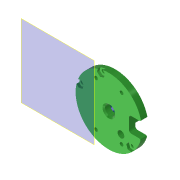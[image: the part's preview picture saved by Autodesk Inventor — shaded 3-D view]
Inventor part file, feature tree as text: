
AUTODESK INVENTOR PART (.ipt)
format: ipt  version: 2022 (Build 260153000, 153)  size: 526,848 bytes
history: native  units: in
note: dims shown in document units (in); Inventor stores cm internally (conversion verified against a paired STEP export)
features: reference x11, extrude x9, sketch x8, other x6, plane x4, projected_geometry x2, fillet x1, chamfer x1
ambient origin geometry x8: Origin, YZ Plane, XZ Plane, XY Plane, X Axis, Y Axis, Z Axis, Center Point
bodies: Solid1 (feature_tree)
feature tree (42):
  plane  "Work Plane1"
  extrude  "Extrusion1"  Depth=0.315in
  extrude  "Extrusion2"  Depth=1.0in
  plane  "Arbeitsebene4"
  extrude  "Extrusion5"  TaperAngle=0.0deg  [1 undecoded]
  plane  "Arbeitsebene3"
  extrude  "Extrusion6"  Depth=0.1102in
  plane  "Arbeitsebene2"
  extrude  "Extrusion7"  Depth=0.0787in
  extrude  "Extrusion10"  Depth=0.0394in TaperAngle=0.0deg
  extrude  "Extrusion11"  Depth=0.3937in
  extrude  "Extrusion12"  Depth=0.0787in
  fillet  "Rundung1"  Radius=0.2165in
  extrude  "Extrusion13"  Depth=0.0787in
  chamfer  "Fase4"  Distance=0.0787in
  sketch  "Sketch1"  dims[d0=0.1969in d1=0.0in d2=0.315in]
  reference  "Reference1"
  reference  "Reference2"
  reference  "Reference3"
  reference  "Reference4"
  reference  "Reference5"
  reference  "Reference6"
  reference  "Reference7"
  reference  "Reference8"
  sketch  "Sketch2"  dims[d3=0.311in d4=1.0in d5=-0.0137in]
  sketch  "Sketch7"  dims[d30=0.1102in d31=0.0in d32=0.0in]
  sketch  "Sketch8"  dims[d33=0.1102in d34=0.1102in]
  sketch  "Sketch9"  dims[d35=0.0in d36=0.0in d37=0.0787in]
  sketch  "Skizze12"  dims[d38=0.0004in d39=0.0in d51=0.0394in d52=0.0in]
  sketch  "Skizze14"  dims[d53=0.2638in d54=0.3937in]
  reference  "Referenz27"
  reference  "Referenz28"
  reference  "Referenz29"
  projected_geometry  "Projizierte Kontur2"
  sketch  "Skizze15"  dims[d55=0.3543in d56=0.0in d60=0.2165in d61=0.2165in d62=0.2165in d63=0.0787in d64=0.0in d65=0.7165in d66=0.7165in d67=0.0787in d68=0.0787in d69=0.3543in d70=0.0in d71=0.315in d72=0.315in d73=0.315in d74=0.315in d75=0.0394in d76=0.0787in d77=45.0deg]
  projected_geometry  "Projizierte Kontur3"
  other  "Assembly1"
  other  "Assembly_MANATEE_V0_Manatee_middle2_v0_18:1"
  other  "Matchboxscope_VCM_v1.iam"
  other  "DIN 912 - ersetzt durch DIN EN ISO 4762 M3 x 25:2"
  other  "DIN 912 - ersetzt durch DIN EN ISO 4762 M3 x 25:1"
  other  "DIN 912 - ersetzt durch DIN EN ISO 4762 M3 x 25:3"
note: 1 required parameter value undecoded (feature->parameter linkage not recoverable at this tier; creation-order binding heuristic only, values carry confidence <= 0.55)
